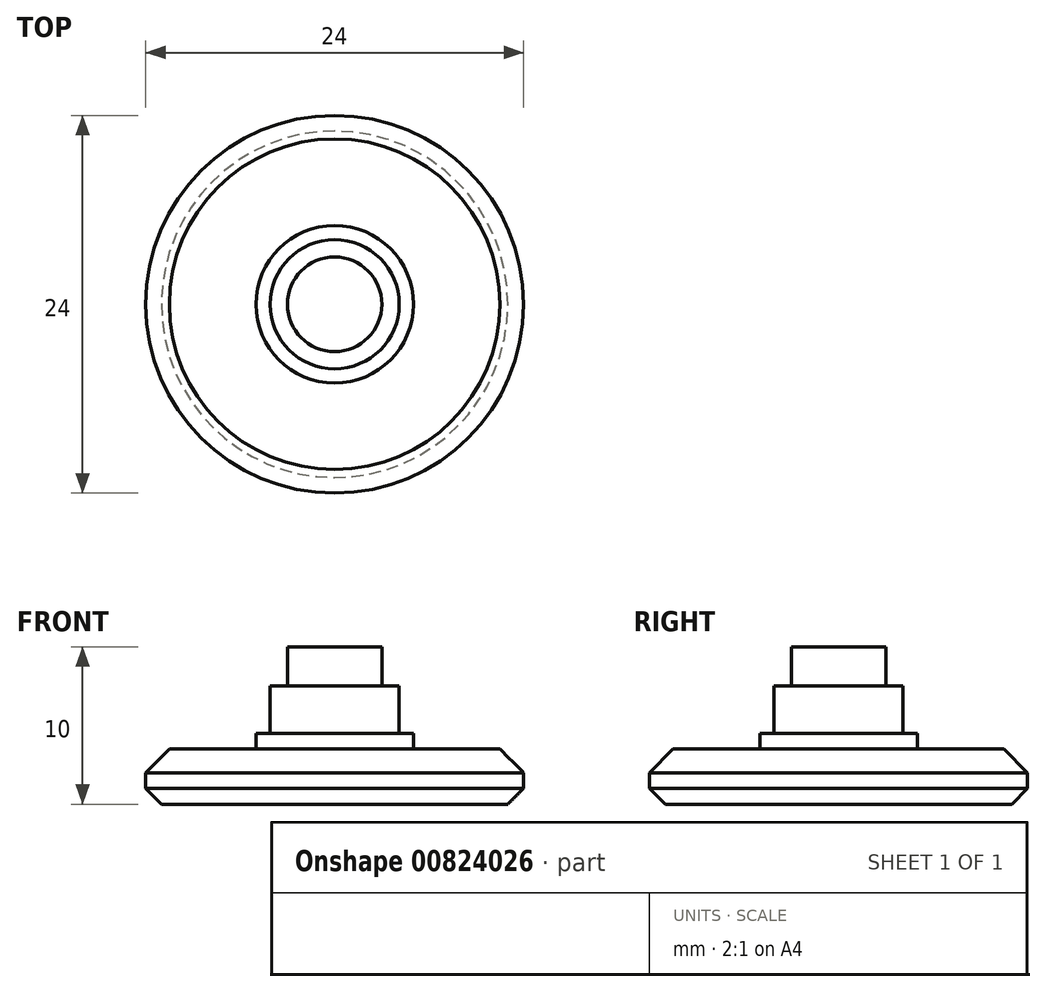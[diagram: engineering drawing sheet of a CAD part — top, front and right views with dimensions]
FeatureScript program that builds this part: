
annotation { "Feature Type Name" : "Feature", "Feature Type Description" : "" }
export const myFeature = defineFeature(function(context is Context, id is Id, definition is map)
    precondition{}
    {
        {
            var Q0;
            Q0=qCreatedBy(makeId("Top.planeOp"),FACE);
            var sketch = newSketch(context, id + "F0", { "sketchPlane" : qUnion([Q0])});
            skCircle(sketch, "E0", {"center": v(0, 0) * mm, "radius": 12 * mm});
            skCircle(sketch, "E1", {"center": v(0, 0) * mm, "radius": 11 * mm});
            skCircle(sketch, "E2", {"center": v(0, 0) * mm, "radius": 4.1 * mm});
            skCircle(sketch, "E3", {"center": v(0, 0) * mm, "radius": 3 * mm});
            skCircle(sketch, "E4", {"center": v(0, 0) * mm, "radius": 5 * mm});
            skSolve(sketch);
        }
        {
            var Q0;
            Q0=makeQuery(id+"F0.imprint","IMPRINT",FACE,{"disambiguationData":[TD([[makeQuery(id+"F0.imprint","IMPRINT",EDGE,{"derivedFrom":sQuery(id+"F0.wireOp",EDGE,"E0")}),1.0]])]});
            var Q1;
            Q1=makeQuery(id+"F0.imprint","IMPRINT",FACE,{"disambiguationData":[TD([[makeQuery(id+"F0.imprint","IMPRINT",EDGE,{"derivedFrom":sQuery(id+"F0.wireOp",EDGE,"E1")}),1.0]])]});
            var Q2;
            Q2=makeQuery(id+"F0.imprint","IMPRINT",FACE,{"disambiguationData":[TD([[makeQuery(id+"F0.imprint","IMPRINT",EDGE,{"derivedFrom":sQuery(id+"F0.wireOp",EDGE,"E3")}),1.0]])]});
            var Q3;
            Q3=makeQuery(id+"F0.imprint","IMPRINT",FACE,{"disambiguationData":[TD([[makeQuery(id+"F0.imprint","IMPRINT",EDGE,{"derivedFrom":sQuery(id+"F0.wireOp",EDGE,"E2")}),1.0]])]});
            var Q4;
            Q4=makeQuery(id+"F0.imprint","IMPRINT",FACE,{"disambiguationData":[TD([[makeQuery(id+"F0.imprint","IMPRINT",EDGE,{"derivedFrom":sQuery(id+"F0.wireOp",EDGE,"E2")}),-1.0]])]});
            extrude(context, id + "F1", {"entities" : qUnion([Q0, Q1, Q2, Q3, Q4]), "depth" : 2 * mm, "offsetDistance" : 25 * mm});
        }
        {
            var Q0;
            Q0=makeQuery(id+"F0.imprint","IMPRINT",FACE,{"disambiguationData":[TD([[makeQuery(id+"F0.imprint","IMPRINT",EDGE,{"derivedFrom":sQuery(id+"F0.wireOp",EDGE,"E1")}),1.0]])]});
            var Q1;
            Q1=makeQuery(id+"F0.imprint","IMPRINT",FACE,{"disambiguationData":[TD([[makeQuery(id+"F0.imprint","IMPRINT",EDGE,{"derivedFrom":sQuery(id+"F0.wireOp",EDGE,"E2")}),1.0]])]});
            var Q2;
            Q2=makeQuery(id+"F0.imprint","IMPRINT",FACE,{"disambiguationData":[TD([[makeQuery(id+"F0.imprint","IMPRINT",EDGE,{"derivedFrom":sQuery(id+"F0.wireOp",EDGE,"E3")}),1.0]])]});
            var Q3;
            Q3=makeQuery(id+"F0.imprint","IMPRINT",FACE,{"disambiguationData":[TD([[makeQuery(id+"F0.imprint","IMPRINT",EDGE,{"derivedFrom":sQuery(id+"F0.wireOp",EDGE,"E2")}),-1.0]])]});
            extrude(context, id + "F2", {"entities" : qUnion([Q0, Q1, Q2, Q3]), "operationType" : NewBodyOperationType.ADD, "depth" : 3.5 * mm, "offsetDistance" : 25 * mm});
        }
        {
            var Q0;
            Q0=makeQuery(id+"F2.boolean.opBoolean","INTERSECT",EDGE,{"derivedFrom":[makeQuery(id+"F1.opExtrude","CAP_FACE",FACE,{"disambiguationData":[OSD([sQuery(id+"F0.wireOp",EDGE,"E0")])],"isStart":false}),makeQuery(id+"F2.opExtrude","SWEPT_FACE",FACE,{"disambiguationData":[OSD([sQuery(id+"F0.wireOp",EDGE,"E1")])]})]});
            chamfer(context, id + "F3", {"entities" : qUnion([Q0]), "width" : 1 * mm, "tangentPropagation" : true});
        }
        {
            var Q0;
            Q0=makeQuery(id+"F0.imprint","IMPRINT",FACE,{"disambiguationData":[TD([[makeQuery(id+"F0.imprint","IMPRINT",EDGE,{"derivedFrom":sQuery(id+"F0.wireOp",EDGE,"E3")}),1.0]])]});
            var Q1;
            Q1=makeQuery(id+"F0.imprint","IMPRINT",FACE,{"disambiguationData":[TD([[makeQuery(id+"F0.imprint","IMPRINT",EDGE,{"derivedFrom":sQuery(id+"F0.wireOp",EDGE,"E2")}),1.0]])]});
            var Q2;
            Q2=makeQuery(id+"F0.imprint","IMPRINT",FACE,{"disambiguationData":[TD([[makeQuery(id+"F0.imprint","IMPRINT",EDGE,{"derivedFrom":sQuery(id+"F0.wireOp",EDGE,"E2")}),-1.0]])]});
            extrude(context, id + "F4", {"entities" : qUnion([Q0, Q1, Q2]), "operationType" : NewBodyOperationType.ADD, "depth" : 4.5 * mm, "offsetDistance" : 25 * mm});
        }
        {
            var Q0;
            Q0=makeQuery(id+"F0.imprint","IMPRINT",FACE,{"disambiguationData":[TD([[makeQuery(id+"F0.imprint","IMPRINT",EDGE,{"derivedFrom":sQuery(id+"F0.wireOp",EDGE,"E2")}),1.0]])]});
            extrude(context, id + "F5", {"entities" : qUnion([Q0]), "operationType" : NewBodyOperationType.ADD, "depth" : 7.5 * mm, "offsetDistance" : 25 * mm});
        }
        {
            var Q0;
            Q0=makeQuery(id+"F0.imprint","IMPRINT",FACE,{"disambiguationData":[TD([[makeQuery(id+"F0.imprint","IMPRINT",EDGE,{"derivedFrom":sQuery(id+"F0.wireOp",EDGE,"E3")}),1.0]])]});
            extrude(context, id + "F6", {"entities" : qUnion([Q0]), "operationType" : NewBodyOperationType.ADD, "depth" : 10 * mm, "offsetDistance" : 25 * mm});
        }
        {
            var Q0;
            Q0=makeQuery(id+"F1.opExtrude","CAP_EDGE",EDGE,{"disambiguationData":[OSD([sQuery(id+"F0.wireOp",EDGE,"E0")])],"isStart":true});
            chamfer(context, id + "F7", {"entities" : qUnion([Q0]), "width" : 1 * mm, "tangentPropagation" : true});
        }
        {
            var Q0;
            Q0=makeQuery(id+"F2.opExtrude","CAP_EDGE",EDGE,{"disambiguationData":[OSD([sQuery(id+"F0.wireOp",EDGE,"E1")])],"isStart":false});
            chamfer(context, id + "F8", {"entities" : qUnion([Q0]), "width" : 0.5 * mm, "tangentPropagation" : true});
        }
    });
